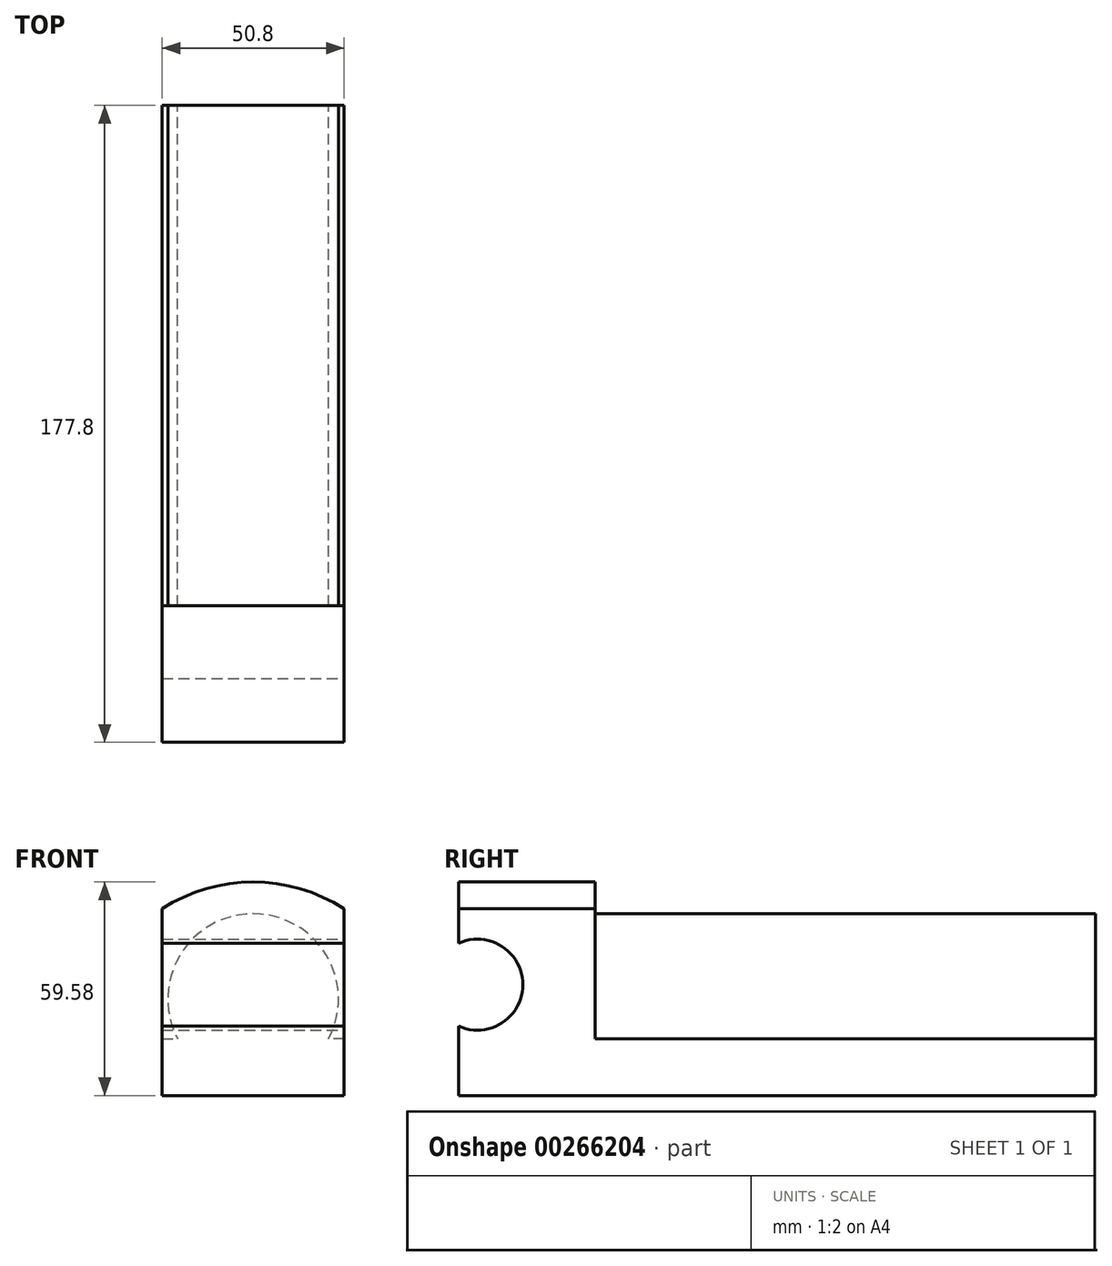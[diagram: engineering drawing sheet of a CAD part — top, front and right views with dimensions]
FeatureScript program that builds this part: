
annotation { "Feature Type Name" : "Feature", "Feature Type Description" : "" }
export const myFeature = defineFeature(function(context is Context, id is Id, definition is map)
    precondition{}
    {
        {
            var Q0;
            Q0=qCreatedBy(makeId("Front.planeOp"),FACE);
            var sketch = newSketch(context, id + "F0", { "sketchPlane" : qUnion([Q0])});
            skLineSegment(sketch, "E0", {"start": v(0, 0) * mm, "end": v(25.4, 0) * mm});
            skLineSegment(sketch, "E1", {"start": v(25.4, 0) * mm, "end": v(25.4, 15.88) * mm});
            skLineSegment(sketch, "E2", {"start": v(-25.4, 15.88) * mm, "end": v(-25.4, 0) * mm});
            skLineSegment(sketch, "E3", {"start": v(-25.4, 0) * mm, "end": v(0, 0) * mm});
            skLineSegment(sketch, "E4", {"start": v(25.4, 15.87) * mm, "end": v(21.1, 15.87) * mm});
            skLineSegment(sketch, "E5", {"start": v(-25.4, 15.88) * mm, "end": v(-21.1, 15.88) * mm});
            skArc(sketch, "E6", {"start": v(21.1, 15.87) * mm, "mid": v(0, 50.74) * mm, "end": v(-21.1, 15.88) * mm});
            skSolve(sketch);
        }
        {
            var Q0;
            Q0 = qSketchRegion(id + "F0", true);
            extrude(context, id + "F1", {"entities" : qUnion([Q0]), "depth" : 139.7 * mm});
        }
        {
            var Q0;
            Q0=makeQuery(id+"F1.opExtrude","CAP_FACE",FACE,{"disambiguationData":[OSD([sQuery(id+"F0.wireOp",EDGE,"E0"),sQuery(id+"F0.wireOp",EDGE,"E1"),sQuery(id+"F0.wireOp",EDGE,"E2"),sQuery(id+"F0.wireOp",EDGE,"E3"),sQuery(id+"F0.wireOp",EDGE,"E4"),sQuery(id+"F0.wireOp",EDGE,"E5"),sQuery(id+"F0.wireOp",EDGE,"E6")])],"isStart":false});
            var sketch = newSketch(context, id + "F2", { "sketchPlane" : qUnion([Q0])});
            skArc(sketch, "E7", {"start": v(25.4, 52.1) * mm, "mid": v(0, 59.58) * mm, "end": v(-25.4, 52.1) * mm});
            skLineSegment(sketch, "E8", {"start": v(-25.4, 0) * mm, "end": v(-25.4, 52.1) * mm});
            skLineSegment(sketch, "E9", {"start": v(25.4, 0) * mm, "end": v(25.4, 52.1) * mm});
            skLineSegment(sketch, "E10", {"start": v(-25.4, 0) * mm, "end": v(25.4, 0) * mm});
            skLineSegment(sketch, "E11", {"start": v(25.4, 52.1) * mm, "end": v(-25.4, 52.1) * mm});
            skSolve(sketch);
        }
        {
            var Q0;
            Q0 = qSketchRegion(id + "F2", true);
            extrude(context, id + "F3", {"entities" : qUnion([Q0]), "operationType" : NewBodyOperationType.ADD, "depth" : 38.1 * mm});
        }
        {
            var Q0;
            Q0=makeQuery(id+"F3.boolean.opBoolean","MERGE",FACE,{"derivedFrom":[makeQuery(id+"F1.opExtrude","SWEPT_FACE",FACE,{"disambiguationData":[OSD([sQuery(id+"F0.wireOp",EDGE,"E1")])]}),makeQuery(id+"F3.opExtrude","SWEPT_FACE",FACE,{"disambiguationData":[OSD([sQuery(id+"F2.wireOp",EDGE,"E9")])]})]});
            var sketch = newSketch(context, id + "F4", { "sketchPlane" : qUnion([Q0])});
            skArc(sketch, "E12", {"start": v(-177.8, 19.35) * mm, "mid": v(-159.91, 30.94) * mm, "end": v(-177.8, 42.52) * mm});
            skSolve(sketch);
        }
        {
            var Q0;
            Q0 = qSketchRegion(id + "F4", true);
            var Q1;
            {var subQ0=sQuery(id+"F4.wireOp",EDGE,"E12");Q1=makeQuery(id+"F4.imprint","IMPRINT",FACE,{"disambiguationData":[TD([[makeQuery(id+"F4.imprint","IMPRINT",EDGE,{"derivedFrom":subQ0}),1.0]])]});}
            extrude(context, id + "F5", {"entities" : qUnion([Q0, Q1]), "operationType" : NewBodyOperationType.REMOVE, "oppositeDirection" : true, "depth" : 50.8 * mm});
        }
    });
